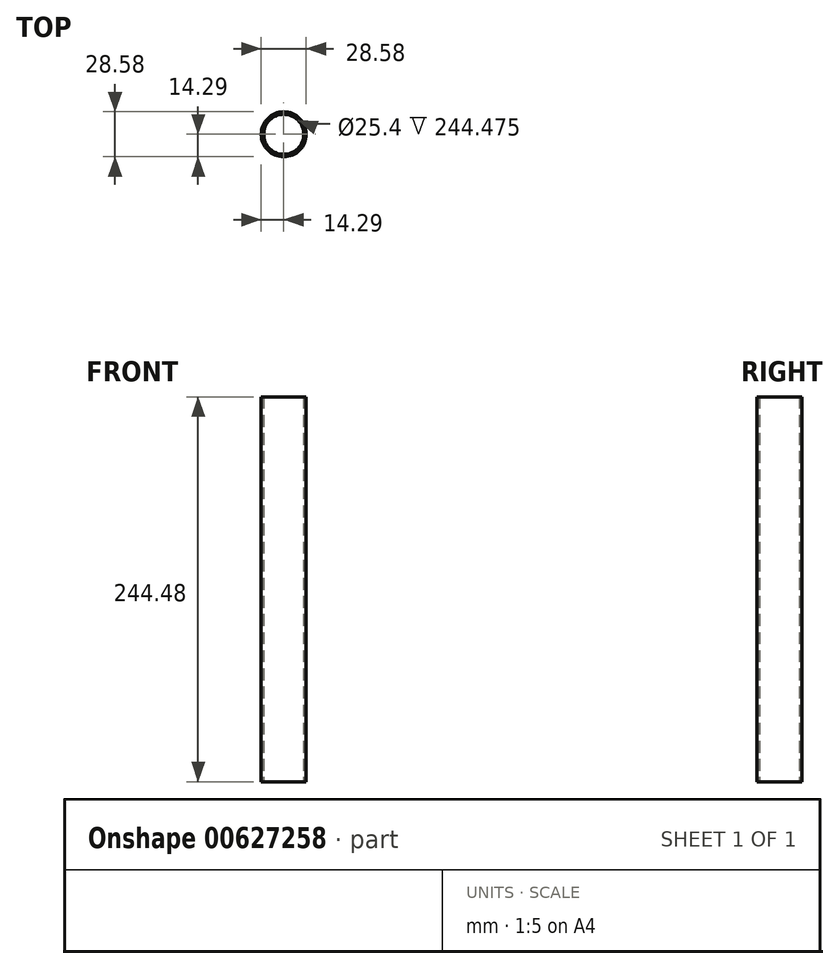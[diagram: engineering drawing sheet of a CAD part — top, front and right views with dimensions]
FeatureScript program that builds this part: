
annotation { "Feature Type Name" : "Feature", "Feature Type Description" : "" }
export const myFeature = defineFeature(function(context is Context, id is Id, definition is map)
    precondition{}
    {
        {
            var Q0;
            Q0=qCreatedBy(makeId("Top.planeOp"),FACE);
            var sketch = newSketch(context, id + "F0", { "sketchPlane" : qUnion([Q0])});
            skLineSegment(sketch, "E0", {"start": v(0, 0) * mm, "end": v(12.7, 0) * mm});
            skCircle(sketch, "E1", {"center": v(0, 0) * mm, "radius": 12.7 * mm});
            skCircle(sketch, "E2.0", {"center": v(0, 0) * mm, "radius": 14.29 * mm});
            skSolve(sketch);
        }
        {
            var Q0;
            Q0=qCreatedBy(makeId("Top.planeOp"),FACE);
            var sketch = newSketch(context, id + "F1", { "sketchPlane" : qUnion([Q0])});
            skSolve(sketch);
        }
        {
            var Q0;
            Q0=qSketchRegion(id+"F1",true);
            var Q1;
            Q1=makeQuery(id+"F0.imprint","IMPRINT",FACE,{"disambiguationData":[TD([[makeQuery(id+"F0.imprint","IMPRINT",EDGE,{"derivedFrom":sQuery(id+"F0.wireOp",EDGE,"E1")}),-1.0]])]});
            extrude(context, id + "F2", {"entities" : qUnion([Q0, Q1]), "depth" : 244.47 * mm, "offsetDistance" : 25.4 * mm});
        }
    });
